# Revit family: Heater-Bromic-Platinum-Electric-Ceiling-Mounted2
name_source: partatom
category: Mechanical Equipment
units: mm (PartAtom-declared; Revit-internal decimal feet)

## family parameters
Classification = None
Cut with Voids When Loaded = Yes
Host = Face
OmniClass Number = 23.75.10.14
OmniClass Title = Independent Electric Heating Units
Part Type = Normal
Room Calculation Point = No
Round Connector Dimension = Use Diameter
Shared = No

## types (1)
- Not a Type - Laod Type Catalog!
    2' Mounting Pole_parameter = Pole : 2' Mounting Pole
    4' Mounting Pole_parameter = Pole : 4' Mounting Pole
    Angle Mounting Pole_parameter = Pole : Angle Mounting Pole
    Apparent Load = 2300 VA
    Approximate Heat Area = 65.00 SF
    Ceiling Mount Pole Profile = Yes
    Default Elevation = 48 "
    Depth = 2 "
    Description = The Platinum Smart-Heat™ Electric excels in efficiency, packing profound performance into a sleek package to suit high-end, style-centric settings. Designed specifically with low-clearance, semi-enclosed and aesthetically-focused spaces in mind, this heater minimizes light emission to blend seamlessly into rooflines with the aid of recess kits or stylishly mount to a number of other surfaces.
    End Clearance = 10 "
    Floor Clearance = 96 "
    Frequency = 50 Hz
    Heater Type Selector = 1
    Length = 33 "
    Load Classification = Power
    Load Sub-Classification Motor = No
    Low Clearance Recess Kit Profile = No
    Low clearance recess kit - 2300W Series = No
    Low clearance recess kit - 3400W Series = No
    Manufacturer = Bromic Heating
    Masking_1 = Yes
    Masking_2 = No
    Masking_3 = No
    Material = Metal-Steel-Stainless-Bromic
    Model = Platinum Smart-Heat™ Electric
    Number of Poles = 1
    Power Factor = 1
    Product data url = https://www.bimobject.com
    ProductCode = ProductCode not specified - Load Type Catalog!
    Screen Material = Ceramic-Tinted-Bromic-Black
    Side Clearance = 10 "
    Standard Mounting Pole_parameter = Pole : Standard Mounting Pole
    Standard Recess Kit Profile = No
    Standard recess kit - 2300W Series = No
    Standard recess kit - 3400W Series = No
    Standard recess kit - 4500W Series = No
    URL = https://www.bromic.com
    Utility = No
    Voltage = 208 V
    Wattage = 2300 W
    Weight = 16.50 lb
    Width = 7 "
    calcDepth = 2 "
    calcLength = 33 "
    calcWidth = 7 "
    recess_depth = 10 "
    recess_length = 73 "
    recess_length/2 = 37 "
    recess_width = 48 "

## geometry (parser evidence)
native form markers: Sweep x16
no freeform markers — native parametric forms only
